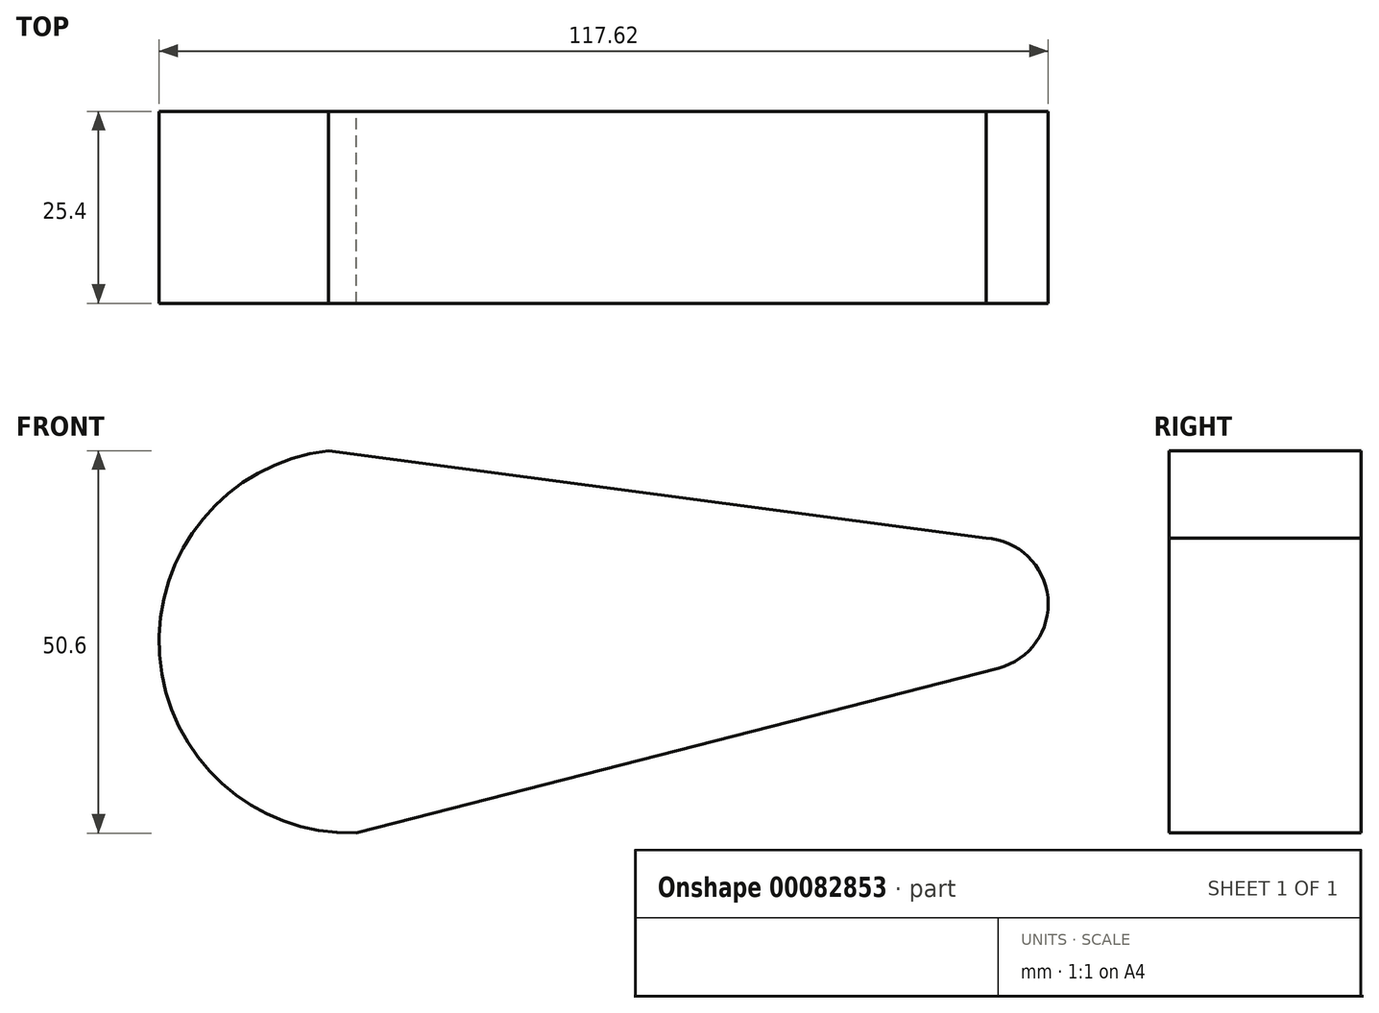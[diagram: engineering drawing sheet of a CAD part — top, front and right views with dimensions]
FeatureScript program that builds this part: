
annotation { "Feature Type Name" : "Feature", "Feature Type Description" : "" }
export const myFeature = defineFeature(function(context is Context, id is Id, definition is map)
    precondition{}
    {
        {
            var Q0;
            Q0=qCreatedBy(makeId("Front.planeOp"),FACE);
            var sketch = newSketch(context, id + "F0", { "sketchPlane" : qUnion([Q0])});
            skArc(sketch, "E0", {"start": v(-45.63, 25.46) * mm, "mid": v(-68, -1.57) * mm, "end": v(-41.99, -25.13) * mm});
            skLineSegment(sketch, "E1", {"start": v(-45.63, 25.46) * mm, "end": v(41.34, 13.88) * mm});
            skLineSegment(sketch, "E2", {"start": v(-41.99, -25.13) * mm, "end": v(42.99, -3.3) * mm});
            skArc(sketch, "E3", {"start": v(42.99, -3.3) * mm, "mid": v(49.51, 6) * mm, "end": v(41.34, 13.88) * mm});
            skSolve(sketch);
        }
        {
            var Q0;
            Q0 = qSketchRegion(id + "F0", true);
            extrude(context, id + "F1", {"entities" : qUnion([Q0]), "depth" : 25.4 * mm});
        }
    });
